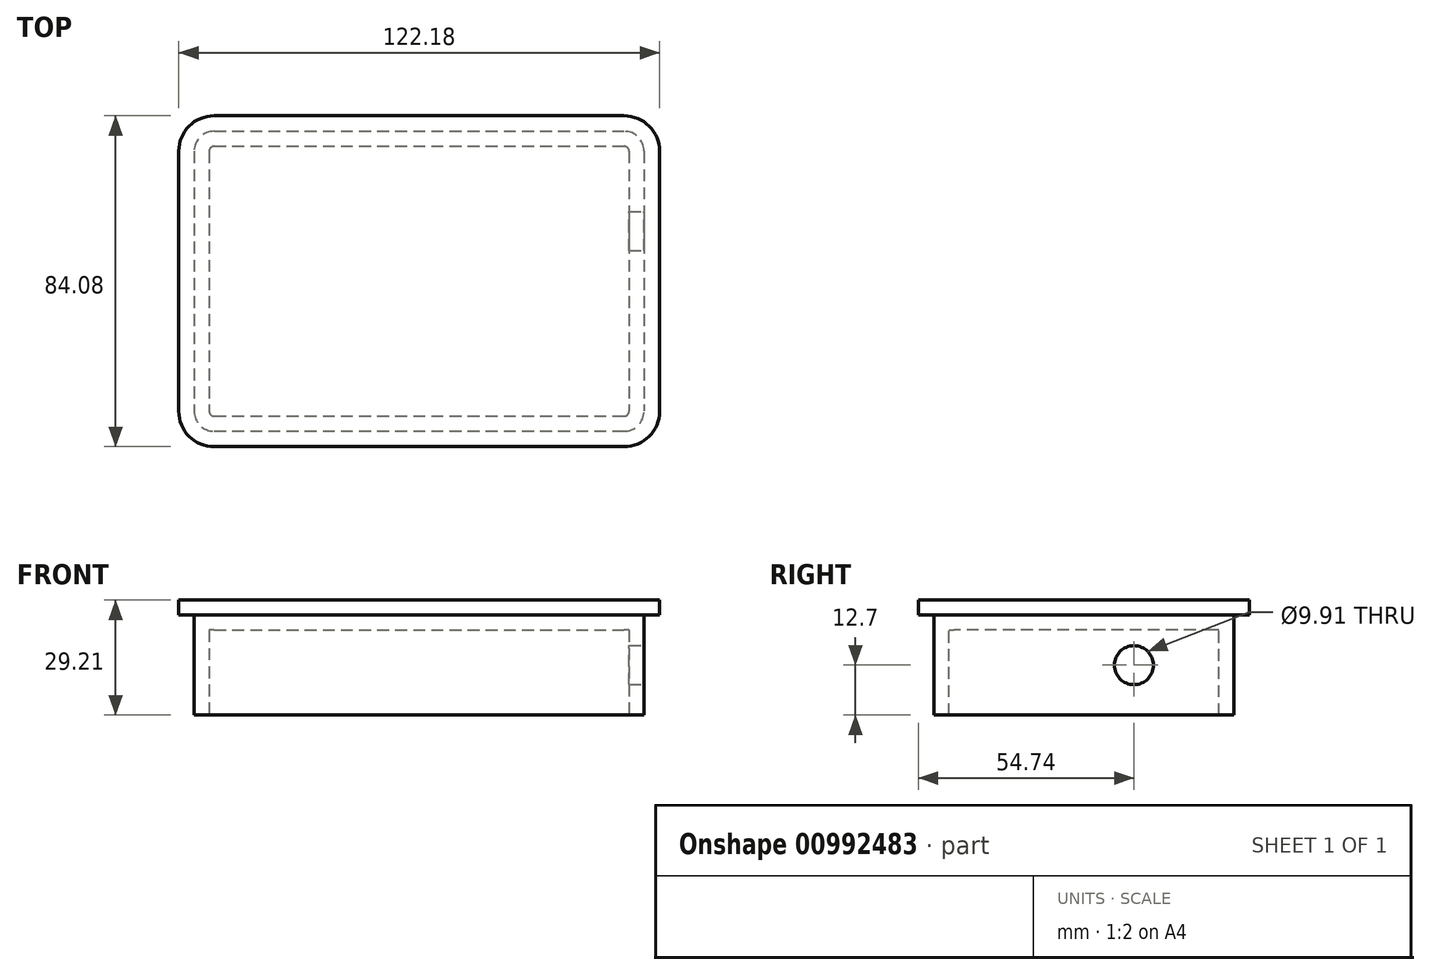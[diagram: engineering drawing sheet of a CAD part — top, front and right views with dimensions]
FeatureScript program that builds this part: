
annotation { "Feature Type Name" : "Feature", "Feature Type Description" : "" }
export const myFeature = defineFeature(function(context is Context, id is Id, definition is map)
    precondition{}
    {
        {
            var Q0;
            Q0=qCreatedBy(makeId("Top.planeOp"),FACE);
            var sketch = newSketch(context, id + "F0", { "sketchPlane" : qUnion([Q0])});
            skLineSegment(sketch, "E0.bottom", {"start": v(0, 0) * mm, "end": v(114.3, 0) * mm});
            skLineSegment(sketch, "E0.top", {"start": v(0, -76.2) * mm, "end": v(114.3, -76.2) * mm});
            skLineSegment(sketch, "E0.left", {"start": v(0, 0) * mm, "end": v(0, -76.2) * mm});
            skLineSegment(sketch, "E0.right", {"start": v(114.3, 0) * mm, "end": v(114.3, -76.2) * mm});
            skSolve(sketch);
        }
        {
            var Q0;
            Q0=makeQuery(id+"F0.imprint","IMPRINT",FACE,{"disambiguationData":[TD([[makeQuery(id+"F0.imprint","IMPRINT",EDGE,{"derivedFrom":sQuery(id+"F0.wireOp",EDGE,"E0.bottom")}),-1.0]])]});
            extrude(context, id + "F1", {"entities" : qUnion([Q0]), "depth" : 25.4 * mm, "offsetDistance" : 25.4 * mm});
        }
        {
            var Q0;
            Q0=makeQuery(id+"F1.opExtrude","SWEPT_EDGE",EDGE,{"disambiguationData":[OSD([sQuery(id+"F0.wireOp",EDGE,"E0.bottom"),sQuery(id+"F0.wireOp",EDGE,"E0.right")])]});
            var Q1;
            Q1=makeQuery(id+"F1.opExtrude","SWEPT_EDGE",EDGE,{"disambiguationData":[OSD([sQuery(id+"F0.wireOp",EDGE,"E0.top"),sQuery(id+"F0.wireOp",EDGE,"E0.right")])]});
            var Q2;
            Q2=makeQuery(id+"F1.opExtrude","SWEPT_EDGE",EDGE,{"disambiguationData":[OSD([sQuery(id+"F0.wireOp",EDGE,"E0.bottom"),sQuery(id+"F0.wireOp",EDGE,"E0.left")])]});
            var Q3;
            Q3=makeQuery(id+"F1.opExtrude","SWEPT_EDGE",EDGE,{"disambiguationData":[OSD([sQuery(id+"F0.wireOp",EDGE,"E0.top"),sQuery(id+"F0.wireOp",EDGE,"E0.left")])]});
            fillet(context, id + "F2", {"entities" : qUnion([Q0, Q1, Q2, Q3]), "radius" : 5.08 * mm, "tangentPropagation" : true, "allowEdgeOverflow" : false});
        }
        {
            var Q0;
            Q0=makeQuery(id+"F1.opExtrude","CAP_FACE",FACE,{"disambiguationData":[OSD([sQuery(id+"F0.wireOp",EDGE,"E0.bottom"),sQuery(id+"F0.wireOp",EDGE,"E0.top"),sQuery(id+"F0.wireOp",EDGE,"E0.left"),sQuery(id+"F0.wireOp",EDGE,"E0.right")])],"isStart":true});
            shell(context, id + "F3", {"entities" : qUnion([Q0]), "thickness" : 3.8 * mm});
        }
        {
            var Q0;
            Q0=makeQuery(id+"F1.opExtrude","SWEPT_FACE",FACE,{"disambiguationData":[OSD([sQuery(id+"F0.wireOp",EDGE,"E0.right")])]});
            var sketch = newSketch(context, id + "F4", { "sketchPlane" : qUnion([Q0])});
            skCircle(sketch, "E1", {"center": v(-25.4, 12.7) * mm, "radius": 4.95 * mm});
            skSolve(sketch);
        }
        {
            var Q0;
            Q0=makeQuery(id+"F4.imprint","IMPRINT",FACE,{"disambiguationData":[TD([[makeQuery(id+"F4.imprint","IMPRINT",EDGE,{"derivedFrom":sQuery(id+"F4.wireOp",EDGE,"E1")}),1.0]])]});
            extrude(context, id + "F5", {"entities" : qUnion([Q0]), "operationType" : NewBodyOperationType.REMOVE, "oppositeDirection" : true, "depth" : 25.4 * mm, "offsetDistance" : 25.4 * mm});
        }
        {
            var Q0;
            Q0=makeQuery(id+"F1.opExtrude","CAP_FACE",FACE,{"disambiguationData":[OSD([sQuery(id+"F0.wireOp",EDGE,"E0.bottom"),sQuery(id+"F0.wireOp",EDGE,"E0.top"),sQuery(id+"F0.wireOp",EDGE,"E0.left"),sQuery(id+"F0.wireOp",EDGE,"E0.right")])],"isStart":false});
            var sketch = newSketch(context, id + "F6", { "sketchPlane" : qUnion([Q0])});
            skArc(sketch, "E2.0.1", {"start": v(0, -71.12) * mm, "mid": v(1.49, -74.71) * mm, "end": v(5.08, -76.2) * mm});
            skLineSegment(sketch, "E2.0.2", {"start": v(5.08, -76.2) * mm, "end": v(109.22, -76.2) * mm});
            skArc(sketch, "E2.0.3", {"start": v(109.22, -76.2) * mm, "mid": v(112.81, -74.71) * mm, "end": v(114.3, -71.12) * mm});
            skLineSegment(sketch, "E2.0.4", {"start": v(114.3, -71.12) * mm, "end": v(114.3, -5.08) * mm});
            skArc(sketch, "E2.0.5", {"start": v(114.3, -5.08) * mm, "mid": v(112.81, -1.49) * mm, "end": v(109.22, 0) * mm});
            skLineSegment(sketch, "E2.0.6", {"start": v(109.22, 0) * mm, "end": v(5.08, 0) * mm});
            skArc(sketch, "E2.0.7", {"start": v(5.08, 0) * mm, "mid": v(1.49, -1.49) * mm, "end": v(0, -5.08) * mm});
            skArc(sketch, "E3.0", {"start": v(5.08, 3.94) * mm, "mid": v(-1.3, 1.3) * mm, "end": v(-3.94, -5.08) * mm});
            skLineSegment(sketch, "E3.1", {"start": v(109.22, 3.94) * mm, "end": v(5.08, 3.94) * mm});
            skLineSegment(sketch, "E3.2", {"start": v(-3.94, -5.08) * mm, "end": v(-3.94, -71.12) * mm});
            skArc(sketch, "E3.3", {"start": v(118.24, -5.08) * mm, "mid": v(115.6, 1.3) * mm, "end": v(109.22, 3.94) * mm});
            skArc(sketch, "E3.4", {"start": v(-3.94, -71.12) * mm, "mid": v(-1.3, -77.5) * mm, "end": v(5.08, -80.14) * mm});
            skLineSegment(sketch, "E3.5", {"start": v(5.08, -80.14) * mm, "end": v(109.22, -80.14) * mm});
            skArc(sketch, "E3.6", {"start": v(109.22, -80.14) * mm, "mid": v(115.6, -77.5) * mm, "end": v(118.24, -71.12) * mm});
            skLineSegment(sketch, "E3.7", {"start": v(118.24, -71.12) * mm, "end": v(118.24, -5.08) * mm});
            skArc(sketch, "E4.0", {"start": v(5.08, 0.13) * mm, "mid": v(1.4, -1.4) * mm, "end": v(-0.13, -5.08) * mm});
            skLineSegment(sketch, "E4.1", {"start": v(109.22, 0.13) * mm, "end": v(5.08, 0.13) * mm});
            skLineSegment(sketch, "E4.2", {"start": v(-0.13, -5.08) * mm, "end": v(-0.13, -71.12) * mm});
            skArc(sketch, "E4.3", {"start": v(114.43, -5.08) * mm, "mid": v(112.9, -1.4) * mm, "end": v(109.22, 0.13) * mm});
            skArc(sketch, "E4.4", {"start": v(-0.13, -71.12) * mm, "mid": v(1.4, -74.8) * mm, "end": v(5.08, -76.33) * mm});
            skLineSegment(sketch, "E4.5", {"start": v(5.08, -76.33) * mm, "end": v(109.22, -76.33) * mm});
            skArc(sketch, "E4.6", {"start": v(109.22, -76.33) * mm, "mid": v(112.9, -74.8) * mm, "end": v(114.43, -71.12) * mm});
            skLineSegment(sketch, "E4.7", {"start": v(114.43, -71.12) * mm, "end": v(114.43, -5.08) * mm});
            skSolve(sketch);
        }
        {
            var Q0;
            Q0=makeQuery(id+"F6.imprint","IMPRINT",FACE,{"disambiguationData":[TD([[makeQuery(id+"F6.imprint","IMPRINT",EDGE,{"derivedFrom":sQuery(id+"F6.wireOp",EDGE,"E3.0")}),1.0]])]});
            var Q1;
            Q1=makeQuery(id+"F6.imprint","IMPRINT",FACE,{"disambiguationData":[TD([[makeQuery(id+"F6.imprint","IMPRINT",EDGE,{"derivedFrom":sQuery(id+"F6.wireOp",EDGE,"E2.0.1")}),-1.0]])]});
            var Q2;
            Q2=makeQuery(id+"F6.imprint","IMPRINT",FACE,{"disambiguationData":[TD([[makeQuery(id+"F6.imprint","IMPRINT",EDGE,{"derivedFrom":sQuery(id+"F6.wireOp",EDGE,"E2.0.1")}),1.0]])]});
            extrude(context, id + "F7", {"entities" : qUnion([Q0, Q1, Q2]), "operationType" : NewBodyOperationType.ADD, "depth" : 3.8 * mm, "offsetDistance" : 25.4 * mm});
        }
    });
